# Revit family: P210059AX-025_AGG222VDW
name_source: partatom
category: Specialty Equipment
units: mm (PartAtom-declared; Revit-internal decimal feet)

## family parameters
Always vertical = Yes
Cut with Voids When Loaded = No
Enable Cutting in Views = No
Maintain Annotation Orientation = No
Part Type = Normal
Room Calculation Point = No
Round Connector Dimension = Use Diameter
Shared = No
Work Plane-Based = No

## types (1)
- AGG222VDW
    Amps = 120 A
    Back Panel Material = ARCAT - Metal - Aluminum
    Body Material = ARCAT - Metal - Steel - White
    Burner Material = ARCAT - Metal - Steel - Stainless
    Clearance Material = ARCAT - Clearance
    Cooking Grid Material = ARCAT - Metal - Steel - Black
    Default Elevation = 0"
    Depth = 26 1/4"
    Description = 20-inch Gas Range with Compact Oven Capacity
    Dimension Guide = https://access.whirlpool.com Guide&sku=AGG222VDW&language=EN
    Door Material = ARCAT - Metal - Steel - White
    Family Name = Gas range
    Feature 1 = Compact Oven Capacity
    Feature 2 = Versatile Cooktop
    Feature 3 = Temp Assure™ Cooking System
    Glass Material = ARCAT - Glass -  Grey
    Handle Material = ARCAT - Metal - Steel - White
    Height = 42"
    Installation-Fabrication = https://access.whirlpool.com Instruction&sku=AGG222VDW&language=EN
    Knob Material = ARCAT - Plastic - White
    Leg Material = ARCAT - Metal - Steel - White
    Lights Material = ARCAT - Plastic - Red
    Manufacturer = Amana
    Model = AGG222VDW
    Voltage = 15 V
    Width = 19 3/4"

## geometry (parser evidence)
native form markers: Sweep x4
no freeform markers — native parametric forms only
